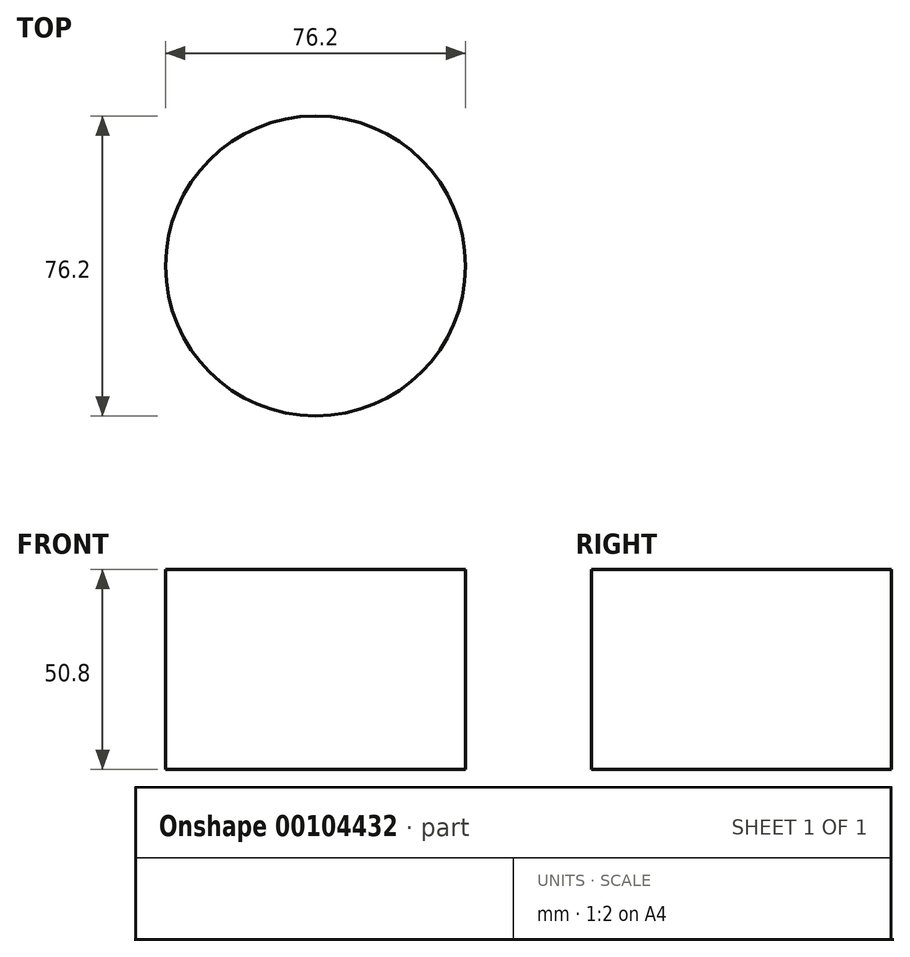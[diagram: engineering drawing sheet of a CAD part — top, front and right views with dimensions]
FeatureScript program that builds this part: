
annotation { "Feature Type Name" : "Feature", "Feature Type Description" : "" }
export const myFeature = defineFeature(function(context is Context, id is Id, definition is map)
    precondition{}
    {
        {
            var Q0;
            Q0=qCreatedBy(makeId("Top.planeOp"),FACE);
            var sketch = newSketch(context, id + "F0", { "sketchPlane" : qUnion([Q0])});
            skCircle(sketch, "E0", {"center": v(0, 0) * mm, "radius": 38.1 * mm});
            skSolve(sketch);
        }
        {
            var Q0;
            Q0 = qSketchRegion(id + "F0", true);
            extrude(context, id + "F1", {"entities" : qUnion([Q0]), "depth" : 50.8 * mm});
        }
    });
